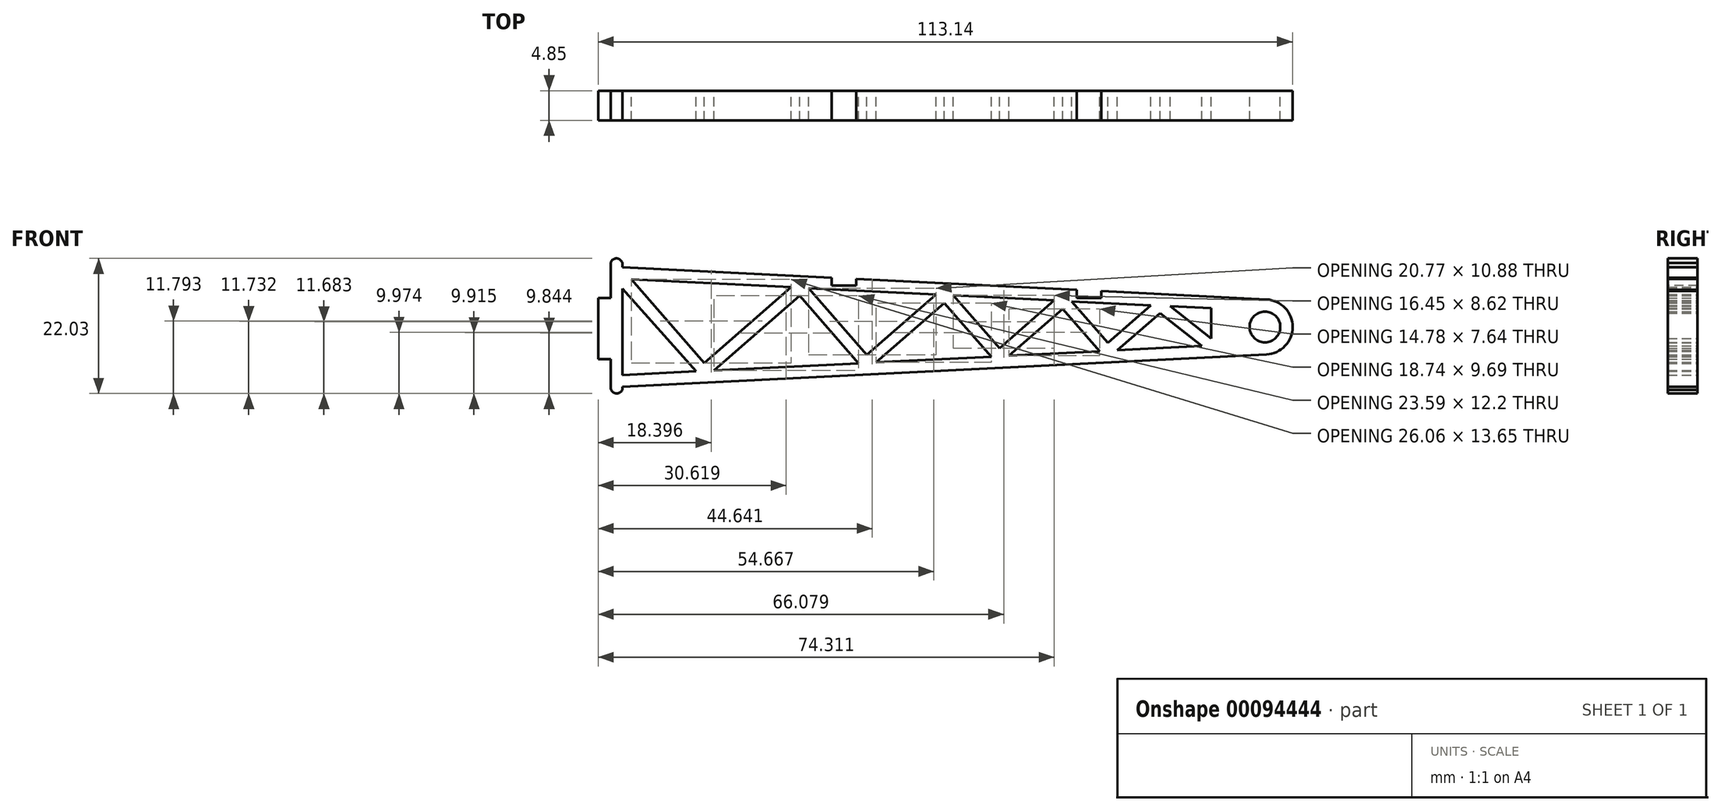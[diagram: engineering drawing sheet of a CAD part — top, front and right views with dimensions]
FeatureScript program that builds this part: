
annotation { "Feature Type Name" : "Feature", "Feature Type Description" : "" }
export const myFeature = defineFeature(function(context is Context, id is Id, definition is map)
    precondition{}
    {
        {
            var Q0;
            Q0=qCreatedBy(makeId("Front.planeOp"),FACE);
            var sketch = newSketch(context, id + "F0", { "sketchPlane" : qUnion([Q0])});
            skLineSegment(sketch, "E0", {"start": v(0, 5) * mm, "end": v(0, 10.1) * mm});
            skLineSegment(sketch, "E1", {"start": v(1.9, 10) * mm, "end": v(101.87, 5) * mm});
            skLineSegment(sketch, "E2", {"start": v(101.87, -4.49) * mm, "end": v(1.9, -9.5) * mm});
            skLineSegment(sketch, "E3", {"start": v(0, -9.59) * mm, "end": v(0, -5) * mm});
            skLineSegment(sketch, "E4", {"start": v(0, 5) * mm, "end": v(-2, 5) * mm});
            skLineSegment(sketch, "E5", {"start": v(-2, 5) * mm, "end": v(-2, -5) * mm});
            skLineSegment(sketch, "E6", {"start": v(-2, -5) * mm, "end": v(0, -5) * mm});
            skLineSegment(sketch, "E7.0", {"start": v(97.85, 3.3) * mm, "end": v(97.85, -1.62) * mm});
            skLineSegment(sketch, "E7.1", {"start": v(3.36, 8.03) * mm, "end": v(29.43, 6.72) * mm});
            skLineSegment(sketch, "E7.2", {"start": v(96.36, -2.86) * mm, "end": v(82.58, -3.55) * mm});
            skLineSegment(sketch, "E7.3", {"start": v(1.9, -7.6) * mm, "end": v(1.9, 0.05) * mm});
            skLineSegment(sketch, "E7.4", {"start": v(1.9, 0.05) * mm, "end": v(1.9, 6.48) * mm});
            skLineSegment(sketch, "E8.0", {"start": v(89.55, 2.53) * mm, "end": v(96.36, -2.86) * mm});
            skLineSegment(sketch, "E8.1", {"start": v(82.58, -3.55) * mm, "end": v(89.55, 2.53) * mm});
            skLineSegment(sketch, "E8.2", {"start": v(73.68, 3.2) * mm, "end": v(79.7, -3.7) * mm});
            skLineSegment(sketch, "E8.3", {"start": v(64.92, -4.44) * mm, "end": v(73.68, 3.2) * mm});
            skLineSegment(sketch, "E8.4", {"start": v(54.4, 4.17) * mm, "end": v(62.04, -4.58) * mm});
            skLineSegment(sketch, "E8.5", {"start": v(1.9, 6.48) * mm, "end": v(13.94, -6.99) * mm});
            skLineSegment(sketch, "E8.6", {"start": v(16.83, -6.84) * mm, "end": v(30.8, 5.35) * mm});
            skLineSegment(sketch, "E8.7", {"start": v(30.8, 5.35) * mm, "end": v(40.41, -5.66) * mm});
            skLineSegment(sketch, "E8.8", {"start": v(43.3, -5.52) * mm, "end": v(54.4, 4.17) * mm});
            skLineSegment(sketch, "E9.0", {"start": v(91.21, 3.63) * mm, "end": v(97.85, -1.62) * mm});
            skLineSegment(sketch, "E9.1", {"start": v(81.04, -2.33) * mm, "end": v(88.05, 3.79) * mm});
            skLineSegment(sketch, "E9.2", {"start": v(75.13, 4.44) * mm, "end": v(81.04, -2.33) * mm});
            skLineSegment(sketch, "E9.3", {"start": v(63.37, -3.22) * mm, "end": v(72.3, 4.58) * mm});
            skLineSegment(sketch, "E9.4", {"start": v(55.85, 5.4) * mm, "end": v(63.37, -3.22) * mm});
            skLineSegment(sketch, "E9.5", {"start": v(3.36, 8.03) * mm, "end": v(15.28, -5.62) * mm});
            skLineSegment(sketch, "E9.6", {"start": v(15.28, -5.62) * mm, "end": v(29.43, 6.72) * mm});
            skLineSegment(sketch, "E9.7", {"start": v(32.25, 6.58) * mm, "end": v(41.75, -4.3) * mm});
            skLineSegment(sketch, "E9.8", {"start": v(41.75, -4.3) * mm, "end": v(53.03, 5.54) * mm});
            skLineSegment(sketch, "E10.trimOffspring", {"start": v(13.94, -6.99) * mm, "end": v(1.9, -7.6) * mm});
            skLineSegment(sketch, "E11.trimOffspring", {"start": v(32.25, 6.58) * mm, "end": v(53.03, 5.54) * mm});
            skLineSegment(sketch, "E12.trimOffspring", {"start": v(40.41, -5.66) * mm, "end": v(16.83, -6.84) * mm});
            skLineSegment(sketch, "E13.trimOffspring", {"start": v(55.85, 5.4) * mm, "end": v(72.3, 4.58) * mm});
            skLineSegment(sketch, "E14.trimOffspring", {"start": v(62.04, -4.58) * mm, "end": v(43.3, -5.52) * mm});
            skLineSegment(sketch, "E15.trimOffspring", {"start": v(75.13, 4.44) * mm, "end": v(88.05, 3.79) * mm});
            skLineSegment(sketch, "E16.trimOffspring", {"start": v(79.7, -3.7) * mm, "end": v(64.92, -4.44) * mm});
            skLineSegment(sketch, "E17.trimOffspring", {"start": v(91.21, 3.63) * mm, "end": v(97.85, 3.3) * mm});
            skPoint(sketch, "E18.orphan", {"position": v(0, 0) * mm});
            skLineSegment(sketch, "E19", {"start": v(1.9, 10) * mm, "end": v(1.9, 10.71) * mm});
            skLineSegment(sketch, "E20", {"start": v(1.9, -9.5) * mm, "end": v(1.9, -10.02) * mm});
            skLineSegment(sketch, "E21", {"start": v(0, -9.59) * mm, "end": v(0, -9.59) * mm});
            skLineSegment(sketch, "E22", {"start": v(0, 10.1) * mm, "end": v(0, 10.48) * mm});
            skArc(sketch, "E23", {"start": v(1.9, 10.71) * mm, "mid": v(0.85, 11.43) * mm, "end": v(0, 10.48) * mm});
            skArc(sketch, "E24", {"start": v(0, -9.59) * mm, "mid": v(0.78, -10.56) * mm, "end": v(1.9, -10.02) * mm});
            skLineSegment(sketch, "E25", {"start": v(101.87, 5) * mm, "end": v(106.87, 4.75) * mm});
            skLineSegment(sketch, "E26", {"start": v(101.87, -4.49) * mm, "end": v(106.87, -4.24) * mm});
            skArc(sketch, "E27", {"start": v(106.87, -4.24) * mm, "mid": v(111.14, 0.26) * mm, "end": v(106.87, 4.75) * mm});
            skCircle(sketch, "E28", {"center": v(106.64, 0.26) * mm, "radius": 2.5 * mm});
            skSolve(sketch);
        }
        {
            var Q0;
            Q0 = qSketchRegion(id + "F0", true);
            extrude(context, id + "F1", {"entities" : qUnion([Q0]), "depth" : 4.85 * mm});
        }
        {
            var Q0;
            Q0=qCreatedBy(makeId("Top.planeOp"),FACE);
            cPlane(context, id + "F2", {"entities" : qUnion([Q0]), "cplaneType" : CPlaneType.OFFSET, "offset" : 10 * mm, "width" : 150 * mm, "height" : 150 * mm});
        }
        {
            var Q0;
            Q0=qCreatedBy(id+"F2.planeOp",FACE);
            var sketch = newSketch(context, id + "F3", { "sketchPlane" : qUnion([Q0])});
            skLineSegment(sketch, "E29.0", {"start": v(1.9, 0) * mm, "end": v(0, 0) * mm});
            skLineSegment(sketch, "E30.0", {"start": v(36, -2.5) * mm, "end": v(36, -5) * mm});
            skLineSegment(sketch, "E30.1", {"start": v(36, -2.5) * mm, "end": v(36, 0) * mm});
            skLineSegment(sketch, "E31.0", {"start": v(76, -2.5) * mm, "end": v(76, -5) * mm});
            skLineSegment(sketch, "E31.1", {"start": v(76, -2.5) * mm, "end": v(76, 0) * mm});
            skLineSegment(sketch, "E32.0", {"start": v(40, -2.5) * mm, "end": v(40, 0) * mm});
            skLineSegment(sketch, "E32.1", {"start": v(40, -2.5) * mm, "end": v(40, -5) * mm});
            skLineSegment(sketch, "E33.0", {"start": v(80, -2.5) * mm, "end": v(80, -5) * mm});
            skLineSegment(sketch, "E33.1", {"start": v(80, -2.5) * mm, "end": v(80, 0) * mm});
            skLineSegment(sketch, "E34", {"start": v(76, -5) * mm, "end": v(80, -5) * mm});
            skLineSegment(sketch, "E35", {"start": v(76, 0) * mm, "end": v(80, 0) * mm});
            skLineSegment(sketch, "E36", {"start": v(36, -5) * mm, "end": v(40, -5) * mm});
            skLineSegment(sketch, "E37", {"start": v(36, 0) * mm, "end": v(40, 0) * mm});
            skSolve(sketch);
        }
        {
            var Q0;
            Q0 = qSketchRegion(id + "F3", true);
            extrude(context, id + "F4", {"entities" : qUnion([Q0]), "operationType" : NewBodyOperationType.REMOVE, "oppositeDirection" : true, "depth" : 3 * mm});
        }
        {
            var Q0;
            Q0=qCreatedBy(id+"F2.planeOp",FACE);
            var sketch = newSketch(context, id + "F5", { "sketchPlane" : qUnion([Q0])});
            skLineSegment(sketch, "E38.0", {"start": v(76, -2.5) * mm, "end": v(76, 0) * mm});
            skLineSegment(sketch, "E39.0", {"start": v(76, -2.5) * mm, "end": v(76, -5) * mm});
            skLineSegment(sketch, "E40.0", {"start": v(76, -5) * mm, "end": v(80, -5) * mm});
            skLineSegment(sketch, "E41.0", {"start": v(80, -2.5) * mm, "end": v(80, -5) * mm});
            skLineSegment(sketch, "E42.0", {"start": v(80, -2.5) * mm, "end": v(80, 0) * mm});
            skLineSegment(sketch, "E43.0", {"start": v(76, 0) * mm, "end": v(80, 0) * mm});
            skSolve(sketch);
        }
        {
            var Q0;
            Q0 = qSketchRegion(id + "F5", true);
            extrude(context, id + "F6", {"entities" : qUnion([Q0]), "operationType" : NewBodyOperationType.REMOVE, "oppositeDirection" : true, "depth" : 5 * mm});
        }
    });
